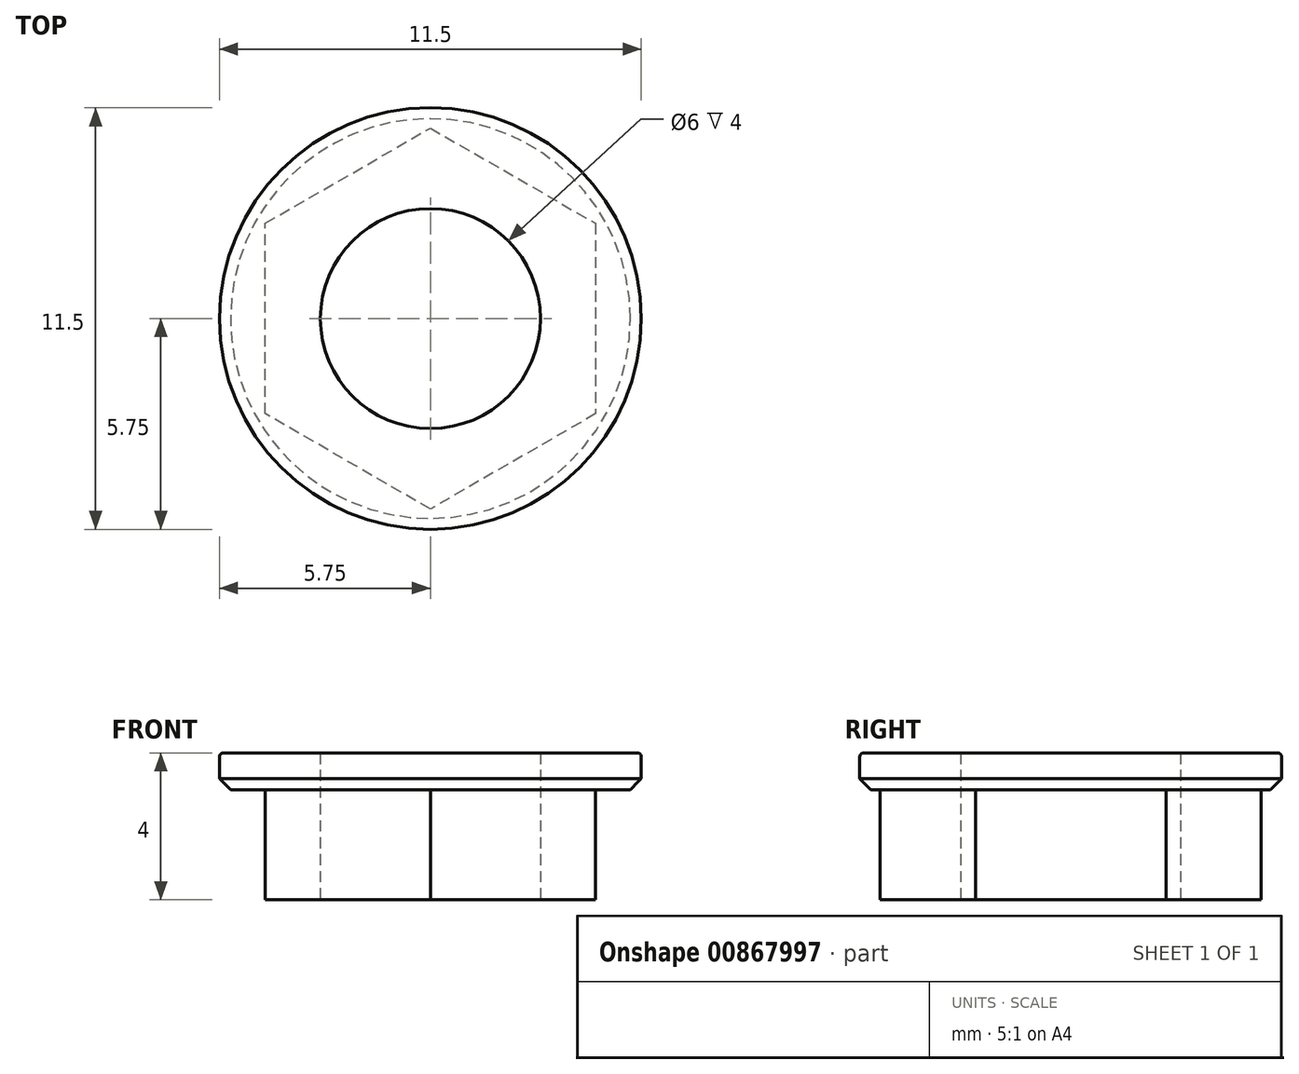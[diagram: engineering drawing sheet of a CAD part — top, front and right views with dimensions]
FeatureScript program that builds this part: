
annotation { "Feature Type Name" : "Feature", "Feature Type Description" : "" }
export const myFeature = defineFeature(function(context is Context, id is Id, definition is map)
    precondition{}
    {
        {
            var Q0;
            Q0=qCreatedBy(makeId("Top.planeOp"),FACE);
            var sketch = newSketch(context, id + "F0", { "sketchPlane" : qUnion([Q0])});
            skCircle(sketch, "E0", {"center": v(0, 0) * mm, "radius": 3 * mm});
            skCircle(sketch, "E1.cCircle", {"center": v(0, 0) * mm, "radius": 4.5 * mm, "construction": true});
            skLineSegment(sketch, "E1.0", {"start": v(4.5, 2.6) * mm, "end": v(4.5, -2.6) * mm});
            skLineSegment(sketch, "E1.1", {"start": v(4.5, -2.6) * mm, "end": v(0, -5.2) * mm});
            skLineSegment(sketch, "E1.2", {"start": v(0, -5.2) * mm, "end": v(-4.5, -2.6) * mm});
            skLineSegment(sketch, "E1.3", {"start": v(-4.5, -2.6) * mm, "end": v(-4.5, 2.6) * mm});
            skLineSegment(sketch, "E1.4", {"start": v(-4.5, 2.6) * mm, "end": v(0, 5.2) * mm});
            skLineSegment(sketch, "E1.5", {"start": v(0, 5.2) * mm, "end": v(4.5, 2.6) * mm});
            skPoint(sketch, "E1.0.midPoint", {"position": v(4.5, 0) * mm});
            skSolve(sketch);
        }
        {
            var Q0;
            Q0 = qSketchRegion(id + "F0", true);
            extrude(context, id + "F1", {"entities" : qUnion([Q0]), "depth" : 3 * mm, "offsetDistance" : 25 * mm});
        }
        {
            var Q0;
            Q0=makeQuery(id+"F1.opExtrude","CAP_FACE",FACE,{"disambiguationData":[OSD([sQuery(id+"F0.wireOp",EDGE,"E0"),sQuery(id+"F0.wireOp",EDGE,"E1.0"),sQuery(id+"F0.wireOp",EDGE,"E1.1"),sQuery(id+"F0.wireOp",EDGE,"E1.2"),sQuery(id+"F0.wireOp",EDGE,"E1.3"),sQuery(id+"F0.wireOp",EDGE,"E1.4"),sQuery(id+"F0.wireOp",EDGE,"E1.5")])],"isStart":false});
            var sketch = newSketch(context, id + "F2", { "sketchPlane" : qUnion([Q0])});
            skCircle(sketch, "E2", {"center": v(0, 0) * mm, "radius": 5.75 * mm});
            skCircle(sketch, "E3", {"center": v(0, 0) * mm, "radius": 3 * mm});
            skSolve(sketch);
        }
        {
            var Q0;
            Q0 = qSketchRegion(id + "F2", true);
            extrude(context, id + "F3", {"entities" : qUnion([Q0]), "operationType" : NewBodyOperationType.ADD, "depth" : 1 * mm, "offsetDistance" : 25 * mm});
        }
        {
            var Q0;
            Q0=makeQuery(id+"F3.opExtrude","CAP_EDGE",EDGE,{"disambiguationData":[OSD([sQuery(id+"F2.wireOp",EDGE,"E2")])],"isStart":true});
            chamfer(context, id + "F4", {"entities" : qUnion([Q0]), "width" : 0.3 * mm, "tangentPropagation" : true});
        }
        {
            var Q0;
            Q0=makeQuery(id+"F3.opExtrude","CAP_EDGE",EDGE,{"disambiguationData":[OSD([sQuery(id+"F2.wireOp",EDGE,"E2")])],"isStart":false});
            fillet(context, id + "F5", {"entities" : qUnion([Q0]), "radius" : 0.1 * mm, "tangentPropagation" : true, "allowEdgeOverflow" : false});
        }
    });
